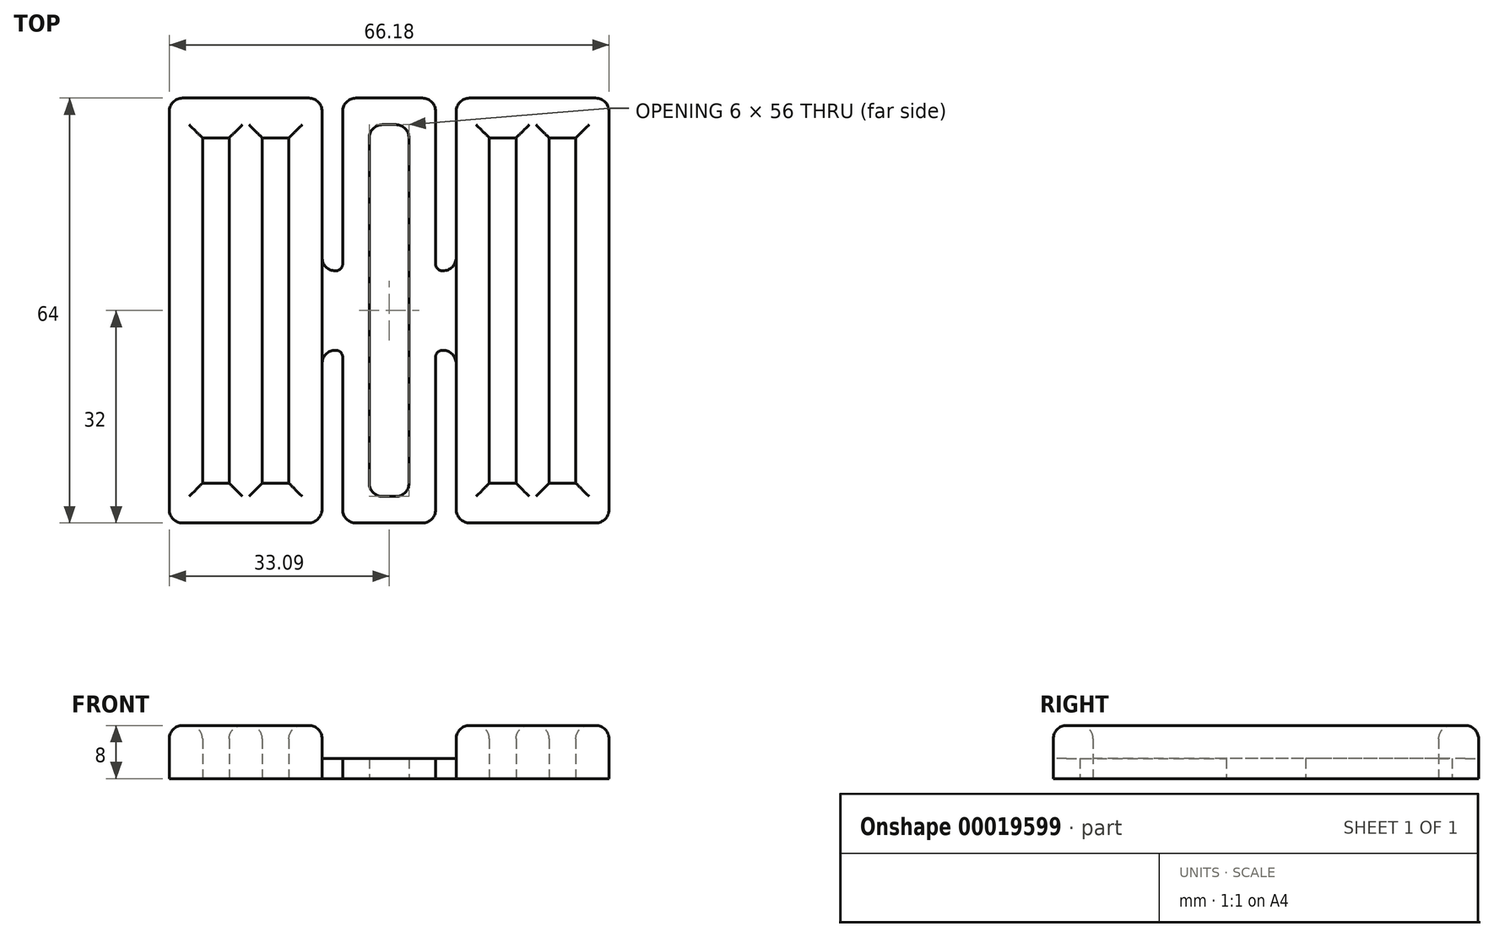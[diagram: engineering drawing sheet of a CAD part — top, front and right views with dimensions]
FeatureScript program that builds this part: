
annotation { "Feature Type Name" : "Feature", "Feature Type Description" : "" }
export const myFeature = defineFeature(function(context is Context, id is Id, definition is map)
    precondition{}
    {
        {
            var Q0;
            Q0=qCreatedBy(makeId("Top.planeOp"),FACE);
            var sketch = newSketch(context, id + "F0", { "sketchPlane" : qUnion([Q0])});
            skLineSegment(sketch, "E0", {"start": v(0, 28) * mm, "end": v(1, 28) * mm});
            skLineSegment(sketch, "E1", {"start": v(3, 26) * mm, "end": v(3, 0) * mm});
            skLineSegment(sketch, "E2", {"start": v(0, 28) * mm, "end": v(0, 32) * mm});
            skLineSegment(sketch, "E3", {"start": v(0, 32) * mm, "end": v(5, 32) * mm});
            skLineSegment(sketch, "E4", {"start": v(7, 30) * mm, "end": v(7, 6.99) * mm});
            skLineSegment(sketch, "E5", {"start": v(8, 5.99) * mm, "end": v(8.09, 5.99) * mm});
            skPoint(sketch, "E6.visualSharp", {"position": v(7, 32) * mm});
            skArc(sketch, "E6.filletArc", {"start": v(7, 30) * mm, "mid": v(6.41, 31.41) * mm, "end": v(5, 32) * mm});
            skPoint(sketch, "E7.visualSharp", {"position": v(3, 28) * mm});
            skArc(sketch, "E7.filletArc", {"start": v(3, 26) * mm, "mid": v(2.41, 27.41) * mm, "end": v(1, 28) * mm});
            skPoint(sketch, "E8.visualSharp", {"position": v(7, 5.99) * mm});
            skArc(sketch, "E8.filletArc", {"start": v(7, 6.99) * mm, "mid": v(7.3, 6.28) * mm, "end": v(8, 5.99) * mm});
            skArc(sketch, "E9.MirrorCS", {"start": v(7, -6.99) * mm, "mid": v(7.3, -6.28) * mm, "end": v(8, -5.99) * mm});
            skLineSegment(sketch, "E10.MirrorCS", {"start": v(3, -26) * mm, "end": v(3, 0) * mm});
            skLineSegment(sketch, "E11.MirrorCS", {"start": v(0, -28) * mm, "end": v(1, -28) * mm});
            skArc(sketch, "E12.MirrorCS", {"start": v(3, -26) * mm, "mid": v(2.41, -27.41) * mm, "end": v(1, -28) * mm});
            skLineSegment(sketch, "E13.MirrorCS", {"start": v(0, -32) * mm, "end": v(5, -32) * mm});
            skLineSegment(sketch, "E14.MirrorCS", {"start": v(7, -30) * mm, "end": v(7, -6.99) * mm});
            skArc(sketch, "E15.MirrorCS", {"start": v(7, -30) * mm, "mid": v(6.41, -31.41) * mm, "end": v(5, -32) * mm});
            skArc(sketch, "E16.MirrorCS", {"start": v(-7, 6.99) * mm, "mid": v(-7.3, 6.28) * mm, "end": v(-8, 5.99) * mm});
            skArc(sketch, "E17.MirrorCS", {"start": v(-3, 26) * mm, "mid": v(-2.41, 27.41) * mm, "end": v(-1, 28) * mm});
            skArc(sketch, "E18.MirrorCS", {"start": v(-7, 30) * mm, "mid": v(-6.41, 31.41) * mm, "end": v(-5, 32) * mm});
            skArc(sketch, "E19.MirrorCS", {"start": v(-7, -6.99) * mm, "mid": v(-7.3, -6.28) * mm, "end": v(-8, -5.99) * mm});
            skLineSegment(sketch, "E20.MirrorCS", {"start": v(0, -28) * mm, "end": v(-1, -28) * mm});
            skLineSegment(sketch, "E21.MirrorCS", {"start": v(0, -32) * mm, "end": v(-5, -32) * mm});
            skArc(sketch, "E22.MirrorCS", {"start": v(-7, -30) * mm, "mid": v(-6.41, -31.41) * mm, "end": v(-5, -32) * mm});
            skPoint(sketch, "E23.MirrorP", {"position": v(-7, 32) * mm});
            skLineSegment(sketch, "E24.MirrorCS", {"start": v(-7, 30) * mm, "end": v(-7, 6.99) * mm});
            skPoint(sketch, "E25.MirrorP", {"position": v(-3, 28) * mm});
            skLineSegment(sketch, "E26.MirrorCS", {"start": v(0, 32) * mm, "end": v(-5, 32) * mm});
            skLineSegment(sketch, "E27.MirrorCS", {"start": v(-3, 26) * mm, "end": v(-3, 0) * mm});
            skLineSegment(sketch, "E28.MirrorCS", {"start": v(-7, -30) * mm, "end": v(-7, -6.99) * mm});
            skLineSegment(sketch, "E29.MirrorCS", {"start": v(-3, -26) * mm, "end": v(-3, 0) * mm});
            skLineSegment(sketch, "E30.MirrorCS", {"start": v(0, 28) * mm, "end": v(-1, 28) * mm});
            skArc(sketch, "E31.MirrorCS", {"start": v(-3, -26) * mm, "mid": v(-2.41, -27.41) * mm, "end": v(-1, -28) * mm});
            skPoint(sketch, "E32.MirrorP", {"position": v(-7, 5.99) * mm});
            skLineSegment(sketch, "E33", {"start": v(10.09, 7.99) * mm, "end": v(10.09, 30) * mm});
            skLineSegment(sketch, "E34", {"start": v(12.09, 32) * mm, "end": v(31.09, 32) * mm});
            skLineSegment(sketch, "E35", {"start": v(33.09, 30) * mm, "end": v(33.09, 0) * mm});
            skLineSegment(sketch, "E36", {"start": v(28.09, 0) * mm, "end": v(28.09, 26) * mm});
            skLineSegment(sketch, "E37", {"start": v(28.09, 26) * mm, "end": v(24.09, 26) * mm});
            skLineSegment(sketch, "E38", {"start": v(24.09, 26) * mm, "end": v(24.09, 0) * mm});
            skLineSegment(sketch, "E39", {"start": v(19.09, 0) * mm, "end": v(19.09, 26) * mm});
            skLineSegment(sketch, "E40", {"start": v(19.09, 26) * mm, "end": v(15.09, 26) * mm});
            skLineSegment(sketch, "E41", {"start": v(15.09, 26) * mm, "end": v(15.09, 0) * mm});
            skPoint(sketch, "E42.visualSharp", {"position": v(10.09, 5.99) * mm});
            skArc(sketch, "E42.filletArc", {"start": v(8.09, 5.99) * mm, "mid": v(9.5, 6.57) * mm, "end": v(10.09, 7.99) * mm});
            skLineSegment(sketch, "E43.MirrorCS", {"start": v(8, -5.99) * mm, "end": v(8.09, -5.99) * mm});
            skLineSegment(sketch, "E44.MirrorCS", {"start": v(19.09, -26) * mm, "end": v(15.09, -26) * mm});
            skLineSegment(sketch, "E45.MirrorCS", {"start": v(19.09, 0) * mm, "end": v(19.09, -26) * mm});
            skLineSegment(sketch, "E46.MirrorCS", {"start": v(15.09, -26) * mm, "end": v(15.09, 0) * mm});
            skLineSegment(sketch, "E47.MirrorCS", {"start": v(33.09, -30) * mm, "end": v(33.09, 0) * mm});
            skLineSegment(sketch, "E48.MirrorCS", {"start": v(28.09, 0) * mm, "end": v(28.09, -26) * mm});
            skLineSegment(sketch, "E49.MirrorCS", {"start": v(24.09, -26) * mm, "end": v(24.09, 0) * mm});
            skLineSegment(sketch, "E50.MirrorCS", {"start": v(10.09, -7.99) * mm, "end": v(10.09, -29.9) * mm});
            skLineSegment(sketch, "E51.MirrorCS", {"start": v(12.19, -32) * mm, "end": v(31.09, -32) * mm});
            skLineSegment(sketch, "E52.MirrorCS", {"start": v(28.09, -26) * mm, "end": v(24.09, -26) * mm});
            skArc(sketch, "E53.MirrorCS", {"start": v(8.09, -5.99) * mm, "mid": v(9.5, -6.57) * mm, "end": v(10.09, -7.99) * mm});
            skPoint(sketch, "E54.MirrorP", {"position": v(10.09, -5.99) * mm});
            skPoint(sketch, "E55.visualSharp", {"position": v(10.09, 32) * mm});
            skArc(sketch, "E55.filletArc", {"start": v(12.09, 32) * mm, "mid": v(10.67, 31.41) * mm, "end": v(10.09, 30) * mm});
            skPoint(sketch, "E56.visualSharp", {"position": v(33.09, 32) * mm});
            skArc(sketch, "E56.filletArc", {"start": v(33.09, 30) * mm, "mid": v(32.5, 31.41) * mm, "end": v(31.09, 32) * mm});
            skPoint(sketch, "E57.visualSharp", {"position": v(33.09, -32) * mm});
            skArc(sketch, "E57.filletArc", {"start": v(31.09, -32) * mm, "mid": v(32.5, -31.41) * mm, "end": v(33.09, -30) * mm});
            skPoint(sketch, "E58.visualSharp", {"position": v(10.09, -32) * mm});
            skArc(sketch, "E58.filletArc", {"start": v(10.09, -29.9) * mm, "mid": v(10.7, -31.38) * mm, "end": v(12.19, -32) * mm});
            skLineSegment(sketch, "E59.MirrorCS", {"start": v(-8, -5.99) * mm, "end": v(-8.09, -5.99) * mm});
            skLineSegment(sketch, "E60.MirrorCS", {"start": v(-8, 5.99) * mm, "end": v(-8.09, 5.99) * mm});
            skArc(sketch, "E61.MirrorCS", {"start": v(-10.09, -29.9) * mm, "mid": v(-10.7, -31.38) * mm, "end": v(-12.19, -32) * mm});
            skArc(sketch, "E62.MirrorCS", {"start": v(-33.09, 30) * mm, "mid": v(-32.5, 31.41) * mm, "end": v(-31.09, 32) * mm});
            skArc(sketch, "E63.MirrorCS", {"start": v(-12.09, 32) * mm, "mid": v(-10.67, 31.41) * mm, "end": v(-10.09, 30) * mm});
            skArc(sketch, "E64.MirrorCS", {"start": v(-31.09, -32) * mm, "mid": v(-32.5, -31.41) * mm, "end": v(-33.09, -30) * mm});
            skLineSegment(sketch, "E65.MirrorCS", {"start": v(-28.09, 0) * mm, "end": v(-28.09, -26) * mm});
            skPoint(sketch, "E66.MirrorP", {"position": v(-10.09, 5.99) * mm});
            skLineSegment(sketch, "E67.MirrorCS", {"start": v(-19.09, 0) * mm, "end": v(-19.09, -26) * mm});
            skPoint(sketch, "E68.MirrorP", {"position": v(-10.09, 32) * mm});
            skLineSegment(sketch, "E69.MirrorCS", {"start": v(-33.09, 30) * mm, "end": v(-33.09, 0) * mm});
            skLineSegment(sketch, "E70.MirrorCS", {"start": v(-12.19, -32) * mm, "end": v(-31.09, -32) * mm});
            skLineSegment(sketch, "E71.MirrorCS", {"start": v(-12.09, 32) * mm, "end": v(-31.09, 32) * mm});
            skLineSegment(sketch, "E72.MirrorCS", {"start": v(-10.09, -7.99) * mm, "end": v(-10.09, -29.9) * mm});
            skPoint(sketch, "E73.MirrorP", {"position": v(-33.09, 32) * mm});
            skPoint(sketch, "E74.MirrorP", {"position": v(-10.09, -5.99) * mm});
            skLineSegment(sketch, "E75.MirrorCS", {"start": v(-15.09, -26) * mm, "end": v(-15.09, 0) * mm});
            skLineSegment(sketch, "E76.MirrorCS", {"start": v(-19.09, 0) * mm, "end": v(-19.09, 26) * mm});
            skLineSegment(sketch, "E77.MirrorCS", {"start": v(-15.09, 26) * mm, "end": v(-15.09, 0) * mm});
            skPoint(sketch, "E78.MirrorP", {"position": v(-10.09, -32) * mm});
            skLineSegment(sketch, "E79.MirrorCS", {"start": v(-33.09, -30) * mm, "end": v(-33.09, 0) * mm});
            skLineSegment(sketch, "E80.MirrorCS", {"start": v(-24.09, 26) * mm, "end": v(-24.09, 0) * mm});
            skArc(sketch, "E81.MirrorCS", {"start": v(-8.09, 5.99) * mm, "mid": v(-9.5, 6.57) * mm, "end": v(-10.09, 7.99) * mm});
            skPoint(sketch, "E82.MirrorP", {"position": v(-33.09, -32) * mm});
            skLineSegment(sketch, "E83.MirrorCS", {"start": v(-28.09, 26) * mm, "end": v(-24.09, 26) * mm});
            skArc(sketch, "E84.MirrorCS", {"start": v(-8.09, -5.99) * mm, "mid": v(-9.5, -6.57) * mm, "end": v(-10.09, -7.99) * mm});
            skLineSegment(sketch, "E85.MirrorCS", {"start": v(-19.09, -26) * mm, "end": v(-15.09, -26) * mm});
            skLineSegment(sketch, "E86.MirrorCS", {"start": v(-24.09, -26) * mm, "end": v(-24.09, 0) * mm});
            skLineSegment(sketch, "E87.MirrorCS", {"start": v(-19.09, 26) * mm, "end": v(-15.09, 26) * mm});
            skLineSegment(sketch, "E88.MirrorCS", {"start": v(-10.09, 7.99) * mm, "end": v(-10.09, 30) * mm});
            skLineSegment(sketch, "E89.MirrorCS", {"start": v(-28.09, 0) * mm, "end": v(-28.09, 26) * mm});
            skLineSegment(sketch, "E90.MirrorCS", {"start": v(-28.09, -26) * mm, "end": v(-24.09, -26) * mm});
            skSolve(sketch);
        }
        {
            var Q0;
            Q0=makeQuery(id+"F0.imprint","IMPRINT",FACE,{"disambiguationData":[TD([[makeQuery(id+"F0.imprint","IMPRINT",EDGE,{"derivedFrom":sQuery(id+"F0.wireOp",EDGE,"E0")}),1.0]])]});
            extrude(context, id + "F1", {"entities" : qUnion([Q0]), "depth" : 3 * mm});
        }
        {
            var Q0;
            Q0=makeQuery(id+"F1.opExtrude","CAP_FACE",FACE,{"disambiguationData":[OSD([sQuery(id+"F0.wireOp",EDGE,"E0"),sQuery(id+"F0.wireOp",EDGE,"E1"),sQuery(id+"F0.wireOp",EDGE,"E3"),sQuery(id+"F0.wireOp",EDGE,"E4"),sQuery(id+"F0.wireOp",EDGE,"E5"),sQuery(id+"F0.wireOp",EDGE,"E6.filletArc"),sQuery(id+"F0.wireOp",EDGE,"E7.filletArc"),sQuery(id+"F0.wireOp",EDGE,"E8.filletArc"),sQuery(id+"F0.wireOp",EDGE,"E9.MirrorCS"),sQuery(id+"F0.wireOp",EDGE,"E10.MirrorCS"),sQuery(id+"F0.wireOp",EDGE,"E11.MirrorCS"),sQuery(id+"F0.wireOp",EDGE,"E12.MirrorCS"),sQuery(id+"F0.wireOp",EDGE,"E13.MirrorCS"),sQuery(id+"F0.wireOp",EDGE,"E14.MirrorCS"),sQuery(id+"F0.wireOp",EDGE,"E15.MirrorCS"),sQuery(id+"F0.wireOp",EDGE,"E16.MirrorCS"),sQuery(id+"F0.wireOp",EDGE,"E17.MirrorCS"),sQuery(id+"F0.wireOp",EDGE,"E18.MirrorCS"),sQuery(id+"F0.wireOp",EDGE,"E19.MirrorCS"),sQuery(id+"F0.wireOp",EDGE,"E20.MirrorCS"),sQuery(id+"F0.wireOp",EDGE,"E21.MirrorCS"),sQuery(id+"F0.wireOp",EDGE,"E22.MirrorCS"),sQuery(id+"F0.wireOp",EDGE,"E24.MirrorCS"),sQuery(id+"F0.wireOp",EDGE,"E26.MirrorCS"),sQuery(id+"F0.wireOp",EDGE,"E27.MirrorCS"),sQuery(id+"F0.wireOp",EDGE,"E28.MirrorCS"),sQuery(id+"F0.wireOp",EDGE,"E29.MirrorCS"),sQuery(id+"F0.wireOp",EDGE,"E30.MirrorCS"),sQuery(id+"F0.wireOp",EDGE,"E31.MirrorCS"),sQuery(id+"F0.wireOp",EDGE,"E33"),sQuery(id+"F0.wireOp",EDGE,"E34"),sQuery(id+"F0.wireOp",EDGE,"E35"),sQuery(id+"F0.wireOp",EDGE,"E36"),sQuery(id+"F0.wireOp",EDGE,"E37"),sQuery(id+"F0.wireOp",EDGE,"E38"),sQuery(id+"F0.wireOp",EDGE,"E39"),sQuery(id+"F0.wireOp",EDGE,"E40"),sQuery(id+"F0.wireOp",EDGE,"E41"),sQuery(id+"F0.wireOp",EDGE,"E42.filletArc"),sQuery(id+"F0.wireOp",EDGE,"E43.MirrorCS"),sQuery(id+"F0.wireOp",EDGE,"E44.MirrorCS"),sQuery(id+"F0.wireOp",EDGE,"E45.MirrorCS"),sQuery(id+"F0.wireOp",EDGE,"E46.MirrorCS"),sQuery(id+"F0.wireOp",EDGE,"E47.MirrorCS"),sQuery(id+"F0.wireOp",EDGE,"E48.MirrorCS"),sQuery(id+"F0.wireOp",EDGE,"E49.MirrorCS"),sQuery(id+"F0.wireOp",EDGE,"E50.MirrorCS"),sQuery(id+"F0.wireOp",EDGE,"E51.MirrorCS"),sQuery(id+"F0.wireOp",EDGE,"E52.MirrorCS"),sQuery(id+"F0.wireOp",EDGE,"E53.MirrorCS"),sQuery(id+"F0.wireOp",EDGE,"E55.filletArc"),sQuery(id+"F0.wireOp",EDGE,"E56.filletArc"),sQuery(id+"F0.wireOp",EDGE,"E57.filletArc"),sQuery(id+"F0.wireOp",EDGE,"E58.filletArc"),sQuery(id+"F0.wireOp",EDGE,"E59.MirrorCS"),sQuery(id+"F0.wireOp",EDGE,"E60.MirrorCS"),sQuery(id+"F0.wireOp",EDGE,"E61.MirrorCS"),sQuery(id+"F0.wireOp",EDGE,"E62.MirrorCS"),sQuery(id+"F0.wireOp",EDGE,"E63.MirrorCS"),sQuery(id+"F0.wireOp",EDGE,"E64.MirrorCS"),sQuery(id+"F0.wireOp",EDGE,"E65.MirrorCS"),sQuery(id+"F0.wireOp",EDGE,"E67.MirrorCS"),sQuery(id+"F0.wireOp",EDGE,"E69.MirrorCS"),sQuery(id+"F0.wireOp",EDGE,"E70.MirrorCS"),sQuery(id+"F0.wireOp",EDGE,"E71.MirrorCS"),sQuery(id+"F0.wireOp",EDGE,"E72.MirrorCS"),sQuery(id+"F0.wireOp",EDGE,"E75.MirrorCS"),sQuery(id+"F0.wireOp",EDGE,"E76.MirrorCS"),sQuery(id+"F0.wireOp",EDGE,"E77.MirrorCS"),sQuery(id+"F0.wireOp",EDGE,"E79.MirrorCS"),sQuery(id+"F0.wireOp",EDGE,"E80.MirrorCS"),sQuery(id+"F0.wireOp",EDGE,"E81.MirrorCS"),sQuery(id+"F0.wireOp",EDGE,"E83.MirrorCS"),sQuery(id+"F0.wireOp",EDGE,"E84.MirrorCS"),sQuery(id+"F0.wireOp",EDGE,"E85.MirrorCS"),sQuery(id+"F0.wireOp",EDGE,"E86.MirrorCS"),sQuery(id+"F0.wireOp",EDGE,"E87.MirrorCS"),sQuery(id+"F0.wireOp",EDGE,"E88.MirrorCS"),sQuery(id+"F0.wireOp",EDGE,"E89.MirrorCS"),sQuery(id+"F0.wireOp",EDGE,"E90.MirrorCS")])],"isStart":false});
            var sketch = newSketch(context, id + "F2", { "sketchPlane" : qUnion([Q0])});
            skLineSegment(sketch, "E91.0", {"start": v(10.09, 7.99) * mm, "end": v(10.09, 30) * mm});
            skArc(sketch, "E92.0", {"start": v(12.09, 32) * mm, "mid": v(10.67, 31.41) * mm, "end": v(10.09, 30) * mm});
            skLineSegment(sketch, "E93.0", {"start": v(12.09, 32) * mm, "end": v(31.09, 32) * mm});
            skArc(sketch, "E94.0", {"start": v(33.09, 30) * mm, "mid": v(32.5, 31.41) * mm, "end": v(31.09, 32) * mm});
            skLineSegment(sketch, "E95.0", {"start": v(33.09, -30) * mm, "end": v(33.09, 30) * mm});
            skArc(sketch, "E96.0", {"start": v(31.09, -32) * mm, "mid": v(32.5, -31.41) * mm, "end": v(33.09, -30) * mm});
            skLineSegment(sketch, "E97.0", {"start": v(12.19, -32) * mm, "end": v(31.09, -32) * mm});
            skArc(sketch, "E98.0", {"start": v(10.09, -29.9) * mm, "mid": v(10.7, -31.38) * mm, "end": v(12.19, -32) * mm});
            skLineSegment(sketch, "E99.0", {"start": v(10.09, -7.99) * mm, "end": v(10.09, -29.9) * mm});
            skLineSegment(sketch, "E100.0", {"start": v(15.09, -26) * mm, "end": v(15.09, 26) * mm});
            skLineSegment(sketch, "E101.0", {"start": v(19.09, 26) * mm, "end": v(15.09, 26) * mm});
            skLineSegment(sketch, "E102.0", {"start": v(19.09, -26) * mm, "end": v(19.09, 26) * mm});
            skLineSegment(sketch, "E103.0", {"start": v(19.09, -26) * mm, "end": v(15.09, -26) * mm});
            skLineSegment(sketch, "E104.0", {"start": v(24.09, -26) * mm, "end": v(24.09, 26) * mm});
            skLineSegment(sketch, "E105.0", {"start": v(28.09, -26) * mm, "end": v(28.09, 26) * mm});
            skLineSegment(sketch, "E106.0", {"start": v(28.09, 26) * mm, "end": v(24.09, 26) * mm});
            skLineSegment(sketch, "E107.0", {"start": v(28.09, -26) * mm, "end": v(24.09, -26) * mm});
            skLineSegment(sketch, "E108", {"start": v(10.09, 7.99) * mm, "end": v(10.09, -7.99) * mm});
            skLineSegment(sketch, "E109.MirrorCS", {"start": v(-28.09, -26) * mm, "end": v(-24.09, -26) * mm});
            skArc(sketch, "E110.MirrorCS", {"start": v(-31.09, -32) * mm, "mid": v(-32.5, -31.41) * mm, "end": v(-33.09, -30) * mm});
            skLineSegment(sketch, "E111.MirrorCS", {"start": v(-28.09, 26) * mm, "end": v(-24.09, 26) * mm});
            skLineSegment(sketch, "E112.MirrorCS", {"start": v(-19.09, -26) * mm, "end": v(-15.09, -26) * mm});
            skLineSegment(sketch, "E113.MirrorCS", {"start": v(-19.09, 26) * mm, "end": v(-15.09, 26) * mm});
            skLineSegment(sketch, "E114.MirrorCS", {"start": v(-33.09, -30) * mm, "end": v(-33.09, 30) * mm});
            skArc(sketch, "E115.MirrorCS", {"start": v(-33.09, 30) * mm, "mid": v(-32.5, 31.41) * mm, "end": v(-31.09, 32) * mm});
            skLineSegment(sketch, "E116.MirrorCS", {"start": v(-12.09, 32) * mm, "end": v(-31.09, 32) * mm});
            skLineSegment(sketch, "E117.MirrorCS", {"start": v(-12.19, -32) * mm, "end": v(-31.09, -32) * mm});
            skArc(sketch, "E118.MirrorCS", {"start": v(-12.09, 32) * mm, "mid": v(-10.67, 31.41) * mm, "end": v(-10.09, 30) * mm});
            skLineSegment(sketch, "E119.MirrorCS", {"start": v(-10.09, 7.99) * mm, "end": v(-10.09, 30) * mm});
            skArc(sketch, "E120.MirrorCS", {"start": v(-10.09, -29.9) * mm, "mid": v(-10.7, -31.38) * mm, "end": v(-12.19, -32) * mm});
            skLineSegment(sketch, "E121.MirrorCS", {"start": v(-28.09, -26) * mm, "end": v(-28.09, 26) * mm});
            skLineSegment(sketch, "E122.MirrorCS", {"start": v(-10.09, -7.99) * mm, "end": v(-10.09, -29.9) * mm});
            skLineSegment(sketch, "E123.MirrorCS", {"start": v(-24.09, -26) * mm, "end": v(-24.09, 26) * mm});
            skLineSegment(sketch, "E124.MirrorCS", {"start": v(-15.09, -26) * mm, "end": v(-15.09, 26) * mm});
            skLineSegment(sketch, "E125.MirrorCS", {"start": v(-19.09, -26) * mm, "end": v(-19.09, 26) * mm});
            skLineSegment(sketch, "E126.MirrorCS", {"start": v(-10.09, 7.99) * mm, "end": v(-10.09, -7.99) * mm});
            skSolve(sketch);
        }
        {
            var Q0;
            Q0 = qSketchRegion(id + "F2", true);
            extrude(context, id + "F3", {"entities" : qUnion([Q0]), "operationType" : NewBodyOperationType.ADD, "depth" : 5 * mm});
        }
        {
            var Q0;
            Q0=makeQuery(id+"F3.opExtrude","CAP_FACE",FACE,{"disambiguationData":[OSD([sQuery(id+"F2.wireOp",EDGE,"E109.MirrorCS"),sQuery(id+"F2.wireOp",EDGE,"E110.MirrorCS"),sQuery(id+"F2.wireOp",EDGE,"E111.MirrorCS"),sQuery(id+"F2.wireOp",EDGE,"E112.MirrorCS"),sQuery(id+"F2.wireOp",EDGE,"E113.MirrorCS"),sQuery(id+"F2.wireOp",EDGE,"E114.MirrorCS"),sQuery(id+"F2.wireOp",EDGE,"E115.MirrorCS"),sQuery(id+"F2.wireOp",EDGE,"E116.MirrorCS"),sQuery(id+"F2.wireOp",EDGE,"E117.MirrorCS"),sQuery(id+"F2.wireOp",EDGE,"E118.MirrorCS"),sQuery(id+"F2.wireOp",EDGE,"E119.MirrorCS"),sQuery(id+"F2.wireOp",EDGE,"E120.MirrorCS"),sQuery(id+"F2.wireOp",EDGE,"E121.MirrorCS"),sQuery(id+"F2.wireOp",EDGE,"E122.MirrorCS"),sQuery(id+"F2.wireOp",EDGE,"E123.MirrorCS"),sQuery(id+"F2.wireOp",EDGE,"E124.MirrorCS"),sQuery(id+"F2.wireOp",EDGE,"E125.MirrorCS"),sQuery(id+"F2.wireOp",EDGE,"E126.MirrorCS")])],"isStart":false});
            var Q1;
            Q1=makeQuery(id+"F3.opExtrude","CAP_FACE",FACE,{"disambiguationData":[OSD([sQuery(id+"F2.wireOp",EDGE,"E91.0"),sQuery(id+"F2.wireOp",EDGE,"E92.0"),sQuery(id+"F2.wireOp",EDGE,"E93.0"),sQuery(id+"F2.wireOp",EDGE,"E94.0"),sQuery(id+"F2.wireOp",EDGE,"E95.0"),sQuery(id+"F2.wireOp",EDGE,"E96.0"),sQuery(id+"F2.wireOp",EDGE,"E97.0"),sQuery(id+"F2.wireOp",EDGE,"E98.0"),sQuery(id+"F2.wireOp",EDGE,"E99.0"),sQuery(id+"F2.wireOp",EDGE,"E100.0"),sQuery(id+"F2.wireOp",EDGE,"E101.0"),sQuery(id+"F2.wireOp",EDGE,"E102.0"),sQuery(id+"F2.wireOp",EDGE,"E103.0"),sQuery(id+"F2.wireOp",EDGE,"E104.0"),sQuery(id+"F2.wireOp",EDGE,"E105.0"),sQuery(id+"F2.wireOp",EDGE,"E106.0"),sQuery(id+"F2.wireOp",EDGE,"E107.0"),sQuery(id+"F2.wireOp",EDGE,"E108")])],"isStart":false});
            fillet(context, id + "F4", {"entities" : qUnion([Q0, Q1]), "radius" : 2 * mm, "tangentPropagation" : true, "allowEdgeOverflow" : false});
        }
    });
